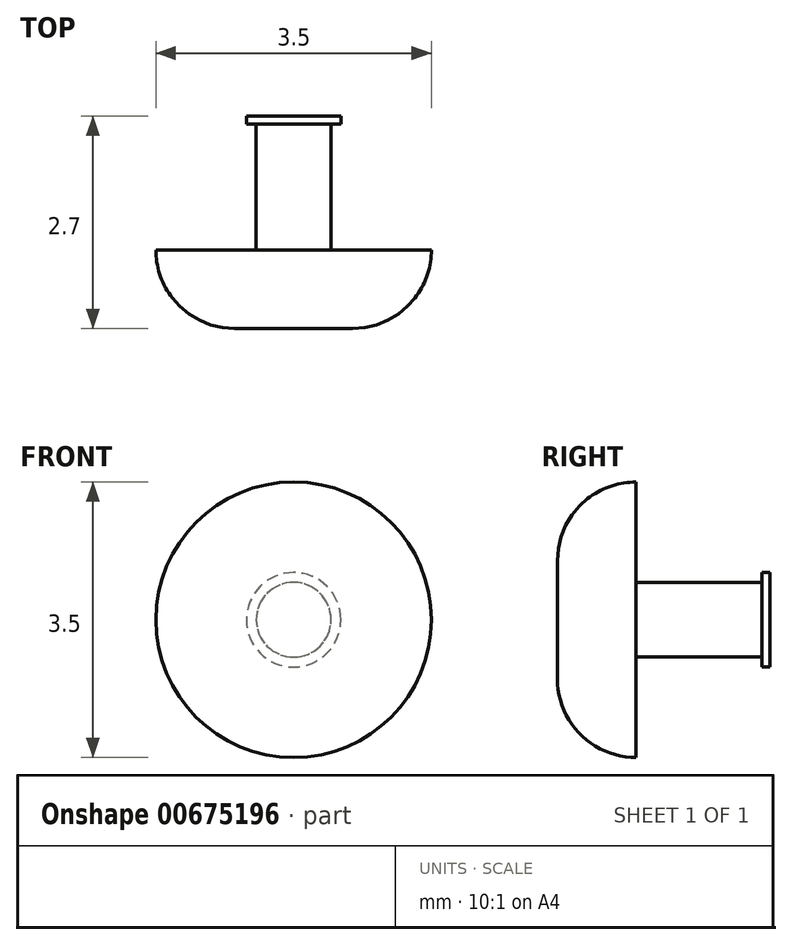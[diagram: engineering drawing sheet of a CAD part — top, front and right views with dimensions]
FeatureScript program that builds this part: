
annotation { "Feature Type Name" : "Feature", "Feature Type Description" : "" }
export const myFeature = defineFeature(function(context is Context, id is Id, definition is map)
    precondition{}
    {
        {
            var Q0;
            Q0=qCreatedBy(makeId("Front.planeOp"),FACE);
            var sketch = newSketch(context, id + "F0", { "sketchPlane" : qUnion([Q0])});
            skCircle(sketch, "E0", {"center": v(0, 0) * mm, "radius": 1.75 * mm});
            skSolve(sketch);
        }
        {
            var Q0;
            Q0 = qSketchRegion(id + "F0", true);
            extrude(context, id + "F1", {"entities" : qUnion([Q0]), "depth" : 1 * mm, "offsetDistance" : 25 * mm});
        }
        {
            var Q0;
            Q0=makeQuery(id+"F1.opExtrude","CAP_EDGE",EDGE,{"disambiguationData":[OSD([sQuery(id+"F0.wireOp",EDGE,"E0")])],"isStart":false});
            fillet(context, id + "F2", {"entities" : qUnion([Q0]), "radius" : 1 * mm, "tangentPropagation" : true, "allowEdgeOverflow" : false});
        }
        {
            var Q0;
            Q0=makeQuery(id+"F1.opExtrude","CAP_FACE",FACE,{"disambiguationData":[OSD([sQuery(id+"F0.wireOp",EDGE,"E0")])],"isStart":true});
            var sketch = newSketch(context, id + "F3", { "sketchPlane" : qUnion([Q0])});
            skCircle(sketch, "E1", {"center": v(0, 0) * mm, "radius": 0.47 * mm});
            skSolve(sketch);
        }
        {
            var Q0;
            Q0 = qSketchRegion(id + "F3", true);
            extrude(context, id + "F4", {"entities" : qUnion([Q0]), "operationType" : NewBodyOperationType.ADD, "depth" : 1.6 * mm, "offsetDistance" : 25 * mm});
        }
        {
            var Q0;
            Q0=makeQuery(id+"F4.opExtrude","CAP_FACE",FACE,{"disambiguationData":[OSD([sQuery(id+"F3.wireOp",EDGE,"E1")])],"isStart":false});
            var sketch = newSketch(context, id + "F5", { "sketchPlane" : qUnion([Q0])});
            skCircle(sketch, "E2", {"center": v(0, 0) * mm, "radius": 0.6 * mm});
            skSolve(sketch);
        }
        {
            var Q0;
            Q0 = qSketchRegion(id + "F5", true);
            extrude(context, id + "F6", {"entities" : qUnion([Q0]), "operationType" : NewBodyOperationType.ADD, "depth" : 0.1 * mm, "offsetDistance" : 25 * mm});
        }
    });
